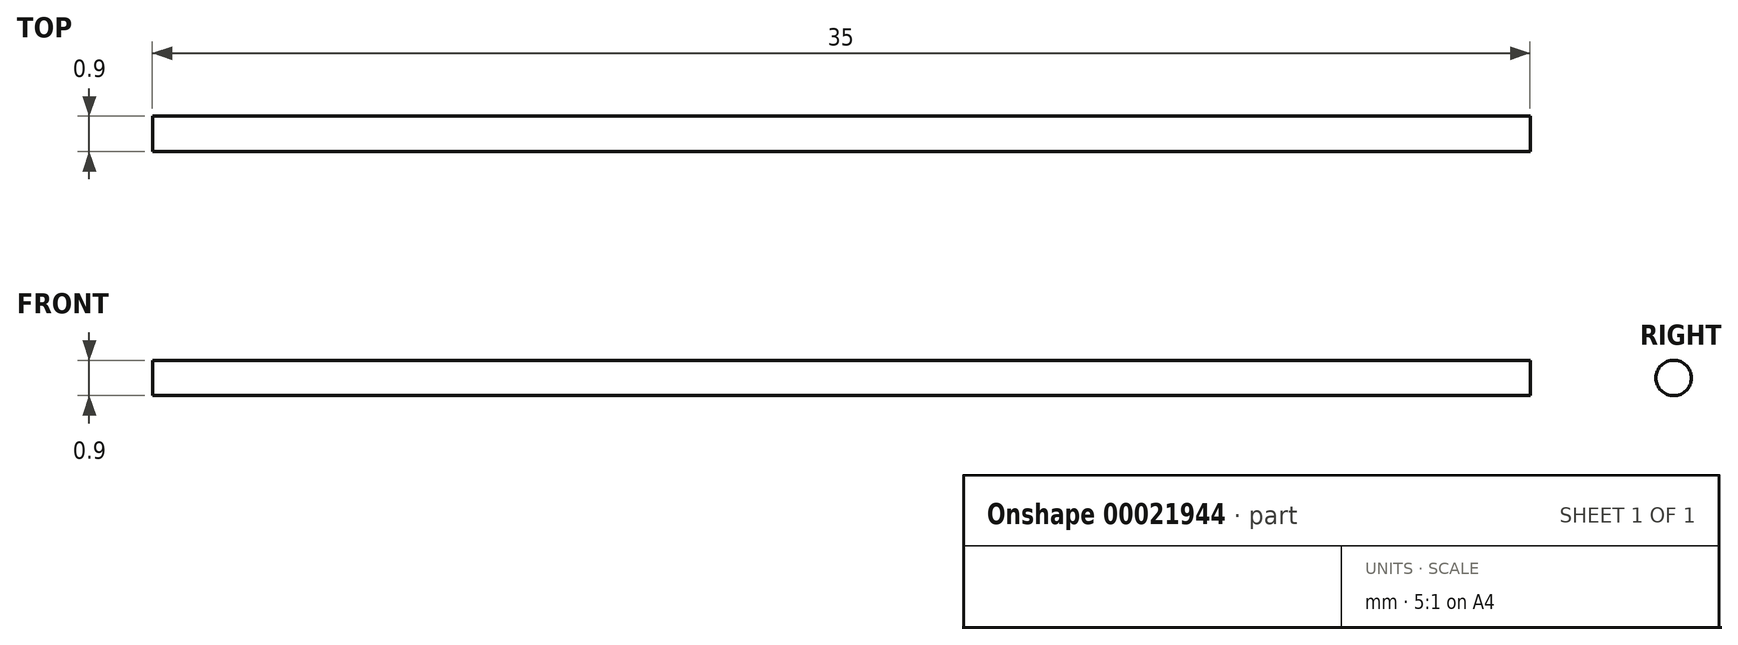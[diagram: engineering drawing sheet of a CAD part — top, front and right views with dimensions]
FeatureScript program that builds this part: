
annotation { "Feature Type Name" : "Feature", "Feature Type Description" : "" }
export const myFeature = defineFeature(function(context is Context, id is Id, definition is map)
    precondition{}
    {
        {
            var Q0;
            Q0=qCreatedBy(makeId("Top.planeOp"),FACE);
            var sketch = newSketch(context, id + "F0", { "sketchPlane" : qUnion([Q0])});
            skLineSegment(sketch, "E0.bottom", {"start": v(-1.1, 0) * mm, "end": v(33.9, 0) * mm});
            skLineSegment(sketch, "E0.top", {"start": v(-1.1, -0.45) * mm, "end": v(33.9, -0.45) * mm});
            skLineSegment(sketch, "E0.left", {"start": v(-1.1, 0) * mm, "end": v(-1.1, -0.45) * mm});
            skLineSegment(sketch, "E0.right", {"start": v(33.9, 0) * mm, "end": v(33.9, -0.45) * mm});
            skSolve(sketch);
        }
        {
            var Q0;
            Q0=makeQuery(id+"F0.imprint","IMPRINT",FACE,{"disambiguationData":[TD([[makeQuery(id+"F0.imprint","IMPRINT",EDGE,{"derivedFrom":sQuery(id+"F0.wireOp",EDGE,"E0.bottom")}),-1.0]])]});
            var Q1;
            Q1=sQuery(id+"F0.wireOp",EDGE,"E0.bottom");
            revolve(context, id + "F1", {"entities" : qUnion([Q0]), "axis" : qUnion([Q1]), "revolveType" : RevolveType.FULL});
        }
    });
